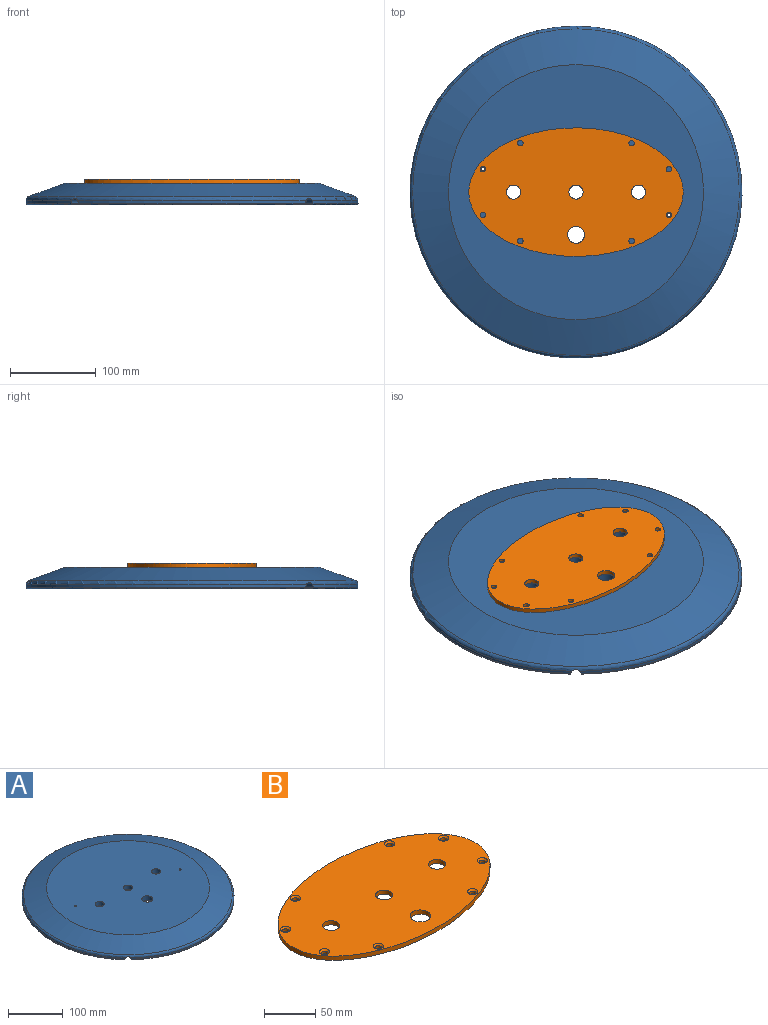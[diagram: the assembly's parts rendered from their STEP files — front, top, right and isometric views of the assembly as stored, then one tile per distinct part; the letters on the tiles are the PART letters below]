
ASSEMBLY  parts=2 mates=1
PART A: 35 faces, bbox 420x420x25 mm
  f0: cylinder r=194mm len=388mm, axis (0,0,-1), area 2817.3mm2, adj f3,f4,f32,f34
  f1: cylinder r=194mm len=267.33mm, axis (0,0,-1), area 915.6mm2, adj f3,f5,f31,f33
  f2: plane 262.91x128.16mm, normal (0,0,-1), area 22010.3mm2, adj f5,f6,f17,f25,f29
  f3: torus R=189mm, axis (0,0,1), area 7373.2mm2, adj f0,f1,f13,f27,f30,f31,f32,f33
  f4: torus R=192mm, axis (0,0,1), area 2823.5mm2, adj f0,f12,f26,f28
  f5: torus R=192mm, axis (0,0,1), area 916mm2, adj f1,f2,f25,f29
  f6: cylinder r=84.5mm len=169mm, axis (0,0,-1), area 7817.3mm2, adj f2,f12,f16,f25,f26,f27,f28,f29
  f7: cylinder r=8.25mm len=16.5mm, axis (0,0,1), area 518.4mm2, adj f11,f16
  f8: cylinder r=8.25mm len=16.5mm, axis (0,0,1), area 518.4mm2, adj f11,f16
  f9: cylinder r=10mm len=20mm, axis (0,0,1), area 628.3mm2, adj f11,f16
  f10: cylinder r=8.25mm len=16.5mm, axis (0,0,1), area 518.4mm2, adj f11,f16
  f11: plane 298x298mm, normal (0,0,1), area 68763.2mm2, adj f7,f8,f9,f10,f13,f14,f15
  f12: plane 384x323.46mm, normal (0,0,-1), area 68584.2mm2, adj f4,f6,f14,f15,f19,f21,f23,f26
  f13: cone r=149mm half-angle=70deg, axis (0,0,-1), area 47371.1mm2, adj f3,f11
  f14: cylinder r=2.1mm len=25mm, axis (0,0,1), area 329.9mm2, adj f11,f12
  f15: cylinder r=2.1mm len=25mm, axis (0,0,1), area 329.9mm2, adj f11,f12
  f16: plane 169x169mm, normal (0,0,-1), area 21476.1mm2, adj f6,f7,f8,f9,f10
  f17: cylinder r=3.75mm len=15mm, axis (0,0,-1), area 353.4mm2, adj f2,f18
  f18: plane 7.5x7.5mm, normal (0,0,-1), area 44.2mm2, adj f17
  f19: cylinder r=3.75mm len=15mm, axis (0,0,-1), area 353.4mm2, adj f12,f20
  f20: plane 7.5x7.5mm, normal (0,0,-1), area 44.2mm2, adj f19
  f21: cylinder r=3.75mm len=15mm, axis (0,0,-1), area 353.4mm2, adj f12,f22
  f22: plane 7.5x7.5mm, normal (0,0,-1), area 44.2mm2, adj f21
  f23: cylinder r=3.75mm len=15mm, axis (0,0,-1), area 353.4mm2, adj f12,f24
  f24: plane 7.5x7.5mm, normal (0,0,-1), area 44.2mm2, adj f23
  f25: plane 77.54x77.54mm, normal (0.71,0.71,0), area 218.4mm2, adj f2,f5,f6,f31
  f26: plane 77.54x77.54mm, normal (-0.71,-0.71,0), area 218.4mm2, adj f4,f6,f12,f32
  f27: plane 78.59x78.59mm, normal (0,0,-1), area 218.3mm2, adj f3,f6,f31,f32
  f28: plane 77.54x77.54mm, normal (0.71,-0.71,0), area 218.4mm2, adj f4,f6,f12,f34
  f29: plane 77.54x77.54mm, normal (-0.71,0.71,0), area 218.4mm2, adj f2,f5,f6,f33
  f30: plane 78.59x78.59mm, normal (0,0,-1), area 218.3mm2, adj f3,f6,f33,f34
  f31: cylinder r=5mm len=81.07mm, axis (-0.71,0.71,0), area 859.6mm2, adj f1,f3,f6,f25,f27
  f32: cylinder r=5mm len=81.07mm, axis (0.71,-0.71,0), area 859.6mm2, adj f0,f3,f6,f26,f27
  f33: cylinder r=5mm len=81.07mm, axis (-0.71,-0.71,0), area 859.6mm2, adj f1,f3,f6,f29,f30
  f34: cylinder r=5mm len=81.07mm, axis (0.71,0.71,0), area 859.6mm2, adj f0,f3,f6,f28,f30
PART B: 23 faces, bbox 250.4x150.3x5 mm
  f0: cylinder r=8.25mm len=16.5mm, axis (0,0,-1), area 259.2mm2, adj f5,f6
  f1: cylinder r=10mm len=20mm, axis (0,0,-1), area 314.2mm2, adj f5,f6
  f2: cylinder r=8.25mm len=16.5mm, axis (0,0,-1), area 259.2mm2, adj f5,f6
  f3: cylinder r=8.25mm len=16.5mm, axis (0,0,-1), area 259.2mm2, adj f5,f6
  f4: extruded ~250.4x150.3mm, area 3196.4mm2, adj f5,f6
  f5: plane 250.4x150.3mm, normal (0,0,1), area 27974.6mm2, adj f0,f1,f2,f3,f4,f8,f10,f12
  f6: plane 250.4x150.3mm, normal (0,0,-1), area 28345.6mm2, adj f0,f1,f2,f3,f4,f7,f9,f11
  f7: cylinder r=3.2mm len=6.4mm, axis (0,0,1), area 64.3mm2, adj f6,f8
  f8: cone r=3.2mm half-angle=45deg, axis (0,0,1), area 65.6mm2, adj f5,f7
  f9: cylinder r=3.2mm len=6.4mm, axis (0,0,1), area 64.3mm2, adj f6,f10
  f10: cone r=3.2mm half-angle=45deg, axis (0,0,1), area 65.6mm2, adj f5,f9
  f11: cylinder r=3.2mm len=6.4mm, axis (0,0,1), area 64.3mm2, adj f6,f12
  f12: cone r=3.2mm half-angle=45deg, axis (0,0,1), area 65.6mm2, adj f5,f11
  f13: cylinder r=3.2mm len=6.4mm, axis (0,0,1), area 64.3mm2, adj f6,f14
  f14: cone r=3.2mm half-angle=45deg, axis (0,0,1), area 65.6mm2, adj f5,f13
  f15: cylinder r=3.2mm len=6.4mm, axis (0,0,1), area 64.3mm2, adj f6,f16
  f16: cone r=3.2mm half-angle=45deg, axis (0,0,1), area 65.6mm2, adj f5,f15
  f17: cylinder r=3.2mm len=6.4mm, axis (0,0,1), area 64.3mm2, adj f6,f18
  f18: cone r=3.2mm half-angle=45deg, axis (0,0,1), area 65.6mm2, adj f5,f17
  f19: cylinder r=3.2mm len=6.4mm, axis (0,0,1), area 64.3mm2, adj f6,f20
  f20: cone r=3.2mm half-angle=45deg, axis (0,0,1), area 65.6mm2, adj f5,f19
  f21: cylinder r=3.2mm len=6.4mm, axis (0,0,1), area 64.3mm2, adj f6,f22
  f22: cone r=3.2mm half-angle=45deg, axis (0,0,1), area 65.6mm2, adj f5,f21
PLACE A at identity
PLACE B rot(axis=(0,1,0),180deg) t=(0,0,30)mm
MATE planar B.f0 <-> A.f7  axis (0,0,-1) through (0,0,25)mm
